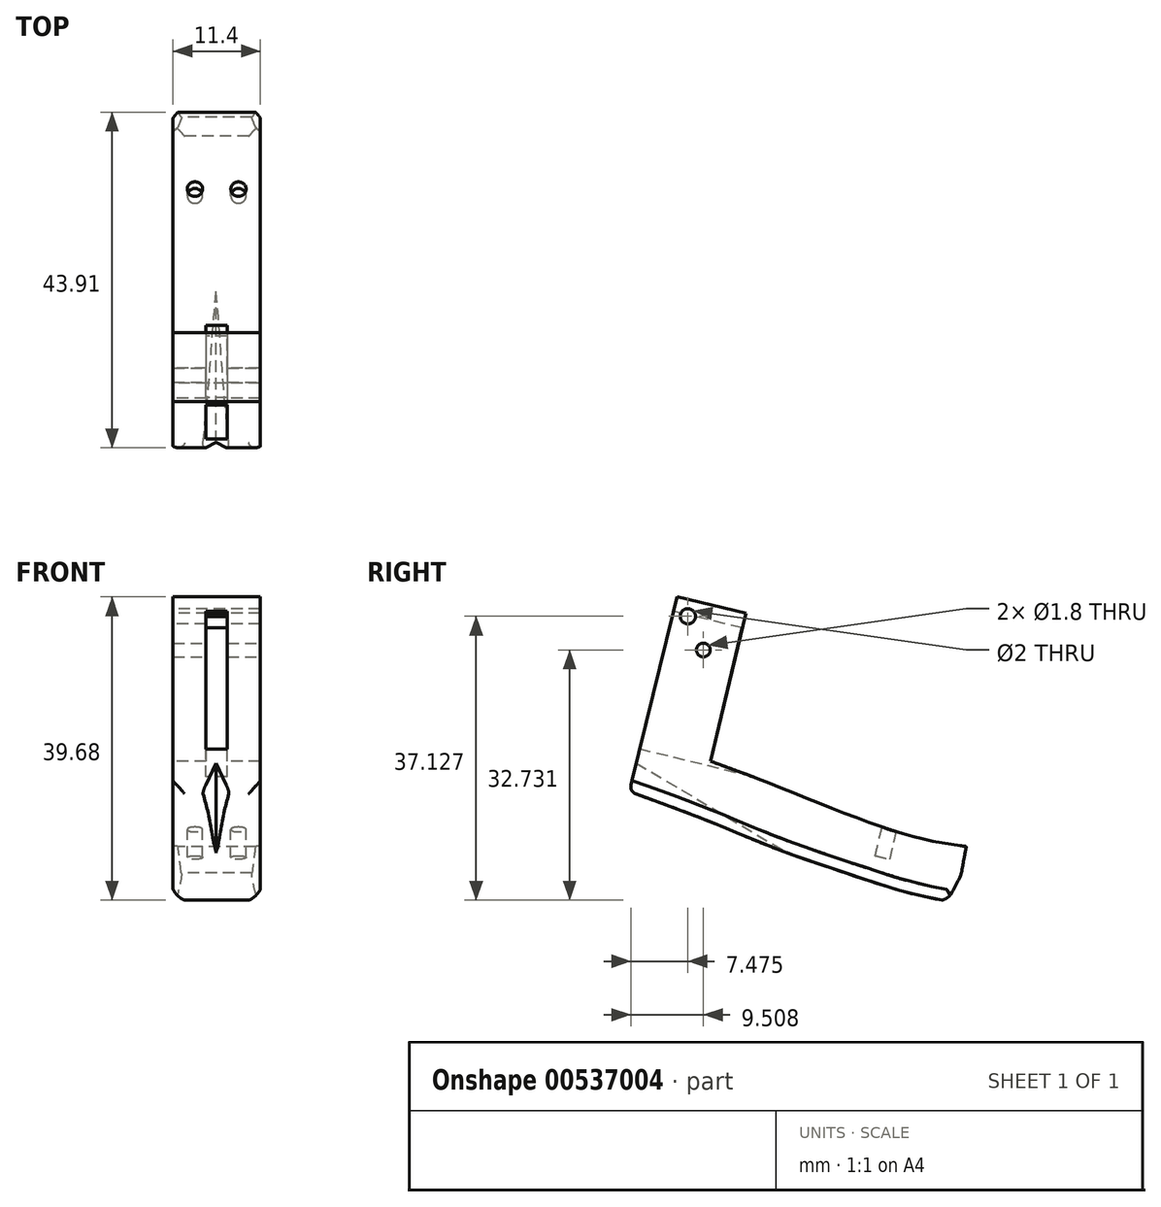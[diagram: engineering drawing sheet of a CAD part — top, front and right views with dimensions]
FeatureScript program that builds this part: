
annotation { "Feature Type Name" : "Feature", "Feature Type Description" : "" }
export const myFeature = defineFeature(function(context is Context, id is Id, definition is map)
    precondition{}
    {
        {
            var Q0;
            Q0=qCreatedBy(makeId("Right.planeOp"),FACE);
            var sketch = newSketch(context, id + "F0", { "sketchPlane" : qUnion([Q0])});
            skLineSegment(sketch, "E0", {"start": v(-10.85, 13.5) * mm, "end": v(-16.58, -9.88) * mm});
            skFitSpline(sketch, "E1", {"points": [v(-16.58, -9.88) * mm, v(-6.61, -13.58) * mm, v(1.68, -16.97) * mm, v(9.59, -19.8) * mm, v(17.55, -22.42) * mm, v(21.87, -23.55) * mm, v(25.94, -24.39) * mm, v(26.4, -22.95) * mm], "startDerivative": vector(48.23, -17.13) * mm, "endDerivative": vector(19.33, 61.07) * mm});
            skLineSegment(sketch, "E2", {"start": v(26.4, -22.95) * mm, "end": v(27.51, -17.06) * mm});
            skFitSpline(sketch, "E3", {"points": [v(27.51, -17.06) * mm, v(20.88, -15.85) * mm, v(10.39, -12.23) * mm, v(-1.4, -7.57) * mm, v(-7.52, -5.36) * mm], "startDerivative": vector(-29.36, 4.09) * mm, "endDerivative": vector(-26.42, 9.18) * mm});
            skLineSegment(sketch, "E4", {"start": v(-10.85, 13.5) * mm, "end": v(-10.35, 15.6) * mm});
            skLineSegment(sketch, "E5", {"start": v(-10.35, 15.6) * mm, "end": v(-1.34, 13.45) * mm});
            skLineSegment(sketch, "E6", {"start": v(-1.34, 13.45) * mm, "end": v(-5.97, -5.9) * mm});
            skCircle(sketch, "E7", {"center": v(-8.93, 13.06) * mm, "radius": 1 * mm});
            skSolve(sketch);
        }
        {
            var Q0;
            Q0=makeQuery(id+"F0.imprint","IMPRINT",FACE,{"disambiguationData":[TD([[makeQuery(id+"F0.imprint","IMPRINT",EDGE,{"derivedFrom":sQuery(id+"F0.wireOp",EDGE,"E0")}),1.0]])]});
            extrude(context, id + "F1", {"entities" : qUnion([Q0]), "depth" : 11.4 * mm, "offsetDistance" : 25 * mm});
        }
        {
            var Q0;
            Q0=makeQuery(id+"F1.opExtrude","SWEPT_FACE",FACE,{"disambiguationData":[OSD([sQuery(id+"F0.wireOp",EDGE,"E0"),sQuery(id+"F0.wireOp",EDGE,"E4")])]});
            var sketch = newSketch(context, id + "F2", { "sketchPlane" : qUnion([Q0])});
            skLineSegment(sketch, "E8", {"start": v(5.7, 10.77) * mm, "end": v(7.1, 10.77) * mm});
            skLineSegment(sketch, "E9", {"start": v(7.1, 10.77) * mm, "end": v(7.1, -7.82) * mm});
            skLineSegment(sketch, "E10", {"start": v(7.1, -7.82) * mm, "end": v(4.3, -7.82) * mm});
            skLineSegment(sketch, "E11", {"start": v(4.3, -7.82) * mm, "end": v(4.3, 10.77) * mm});
            skLineSegment(sketch, "E12", {"start": v(4.3, 10.77) * mm, "end": v(5.7, 10.77) * mm});
            skLineSegment(sketch, "E13", {"start": v(4.3, -5.3) * mm, "end": v(0, -5.3) * mm});
            skSolve(sketch);
        }
        {
            var Q0;
            Q0=makeQuery(id+"F2.imprint","IMPRINT",FACE,{"disambiguationData":[TD([[makeQuery(id+"F2.imprint","IMPRINT",EDGE,{"derivedFrom":sQuery(id+"F2.wireOp",EDGE,"E8")}),-1.0]])]});
            var Q1;
            {var subQ4=sQuery(id+"F2.wireOp",EDGE,"E10");Q1=makeQuery(id+"F2.imprint","IMPRINT",FACE,{"disambiguationData":[TD([[makeQuery(id+"F2.imprint","IMPRINT",EDGE,{"derivedFrom":subQ4}),-1.0]])]});}
            extrude(context, id + "F3", {"entities" : qUnion([Q0, Q1]), "operationType" : NewBodyOperationType.REMOVE, "oppositeDirection" : true, "depth" : 25 * mm, "offsetDistance" : 25 * mm});
        }
        {
            var Q0;
            Q0=makeQuery(id+"F3.boolean.opBoolean","COPY",FACE,{"derivedFrom":makeQuery(id+"F3.opExtrude","SWEPT_FACE",FACE,{"disambiguationData":[OSD([sQuery(id+"F2.wireOp",EDGE,"E11")])]})});
            var sketch = newSketch(context, id + "F4", { "sketchPlane" : qUnion([Q0])});
            skLineSegment(sketch, "E14", {"start": v(-10.8, 13.74) * mm, "end": v(-5.94, 12.55) * mm});
            skLineSegment(sketch, "E15", {"start": v(-5.94, 12.55) * mm, "end": v(-6.9, 8.66) * mm});
            skCircle(sketch, "E16", {"center": v(-6.9, 8.66) * mm, "radius": 0.9 * mm});
            skSolve(sketch);
        }
        {
            var Q0;
            Q0 = qSketchRegion(id + "F4", true);
            extrude(context, id + "F5", {"entities" : qUnion([Q0]), "operationType" : NewBodyOperationType.REMOVE, "endBound" : BoundingType.SYMMETRIC, "oppositeDirection" : true, "depth" : 25 * mm, "offsetDistance" : 25 * mm});
        }
        {
            var Q0;
            Q0=makeQuery(id+"F1.opExtrude","CAP_EDGE",EDGE,{"disambiguationData":[OSD([sQuery(id+"F0.wireOp",EDGE,"E1")])],"isStart":false});
            var Q1;
            Q1=makeQuery(id+"F1.opExtrude","CAP_EDGE",EDGE,{"disambiguationData":[OSD([sQuery(id+"F0.wireOp",EDGE,"E1")])],"isStart":true});
            fillet(context, id + "F6", {"entities" : qUnion([Q0, Q1]), "radius" : 1.5 * mm, "tangentPropagation" : true, "rho" : .1, "crossSection" : FilletCrossSection.CONIC, "allowEdgeOverflow" : false});
        }
        {
            var Q0;
            Q0=makeQuery(id+"F1.opExtrude","SWEPT_EDGE",EDGE,{"disambiguationData":[OSD([sQuery(id+"F0.wireOp",EDGE,"E0"),sQuery(id+"F0.wireOp",EDGE,"E1")])]});
            fillet(context, id + "F7", {"entities" : qUnion([Q0]), "radius" : 1 * mm, "allowEdgeOverflow" : false});
        }
        {
            var Q0;
            Q0=makeQuery(id+"F1.opExtrude","SWEPT_FACE",FACE,{"disambiguationData":[OSD([sQuery(id+"F0.wireOp",EDGE,"E5")])]});
            var sketch = newSketch(context, id + "F8", { "sketchPlane" : qUnion([Q0])});
            skLineSegment(sketch, "E17", {"start": v(5.7, -4.44) * mm, "end": v(5.7, 20.4) * mm});
            skCircle(sketch, "E18", {"center": v(2.85, 20.4) * mm, "radius": 1 * mm});
            skCircle(sketch, "E19", {"center": v(8.55, 20.4) * mm, "radius": 1 * mm});
            skSolve(sketch);
        }
        {
            var Q0;
            Q0 = qSketchRegion(id + "F8", true);
            extrude(context, id + "F9", {"entities" : qUnion([Q0]), "operationType" : NewBodyOperationType.REMOVE, "oppositeDirection" : true, "depth" : 26.9 * mm, "offsetDistance" : 25 * mm});
        }
        {
            var Q0;
            Q0=makeQuery(id+"F1.opExtrude","CAP_FACE",FACE,{"disambiguationData":[OSD([sQuery(id+"F0.wireOp",EDGE,"E0"),sQuery(id+"F0.wireOp",EDGE,"E1"),sQuery(id+"F0.wireOp",EDGE,"E2"),sQuery(id+"F0.wireOp",EDGE,"E3"),sQuery(id+"F0.wireOp",EDGE,"E4"),sQuery(id+"F0.wireOp",EDGE,"E5"),sQuery(id+"F0.wireOp",EDGE,"E6"),sQuery(id+"F0.wireOp",EDGE,"E7")])],"isStart":false});
            var sketch = newSketch(context, id + "F10", { "sketchPlane" : qUnion([Q0])});
            skLineSegment(sketch, "E20", {"start": v(-14.98, -6.24) * mm, "end": v(-8.61, 4.47) * mm});
            skSolve(sketch);
        }
        {
            var Q0;
            Q0=qCreatedBy(makeId("Top.planeOp"),FACE);
            var Q1;
            Q1=sQuery(id+"F10.wireOp",EDGE,"E20");
            cPlane(context, id + "F11", {"entities" : qUnion([Q0, Q1]), "cplaneType" : CPlaneType.LINE_ANGLE, "offset" : 25 * mm, "angle" : 0 * degree, "width" : 150 * mm, "height" : 150 * mm});
        }
        {
            var Q0;
            Q0=qCreatedBy(id+"F11.planeOp",FACE);
            var sketch = newSketch(context, id + "F12", { "sketchPlane" : qUnion([Q0])});
            skLineSegment(sketch, "E21", {"start": v(-5.63, -13.29) * mm, "end": v(-0.99, -22.83) * mm});
            skLineSegment(sketch, "E22", {"start": v(-0.99, -22.83) * mm, "end": v(-11.37, -22.83) * mm});
            skLineSegment(sketch, "E23", {"start": v(-5.63, -13.29) * mm, "end": v(-10.13, -22.83) * mm});
            skSolve(sketch);
        }
        {
            var Q0;
            Q0 = qSketchRegion(id + "F12", true);
            extrude(context, id + "F13", {"entities" : qUnion([Q0]), "operationType" : NewBodyOperationType.REMOVE, "endBound" : BoundingType.SYMMETRIC, "oppositeDirection" : true, "depth" : 149.4 * mm, "offsetDistance" : 25 * mm});
        }
        {
            var Q0;
            Q0=makeQuery(id+"F1.opExtrude","CAP_FACE",FACE,{"disambiguationData":[OSD([sQuery(id+"F0.wireOp",EDGE,"E0"),sQuery(id+"F0.wireOp",EDGE,"E1"),sQuery(id+"F0.wireOp",EDGE,"E2"),sQuery(id+"F0.wireOp",EDGE,"E3"),sQuery(id+"F0.wireOp",EDGE,"E4"),sQuery(id+"F0.wireOp",EDGE,"E5"),sQuery(id+"F0.wireOp",EDGE,"E6"),sQuery(id+"F0.wireOp",EDGE,"E7")])],"isStart":true});
            var sketch = newSketch(context, id + "F14", { "sketchPlane" : qUnion([Q0])});
            skFitSpline(sketch, "E24", {"points": [v(-26.87, -20.46) * mm, v(-25.97, -22.42) * mm, v(-25.08, -23.72) * mm, v(-22.73, -24.43) * mm, v(-19.82, -24.7) * mm], "startDerivative": vector(2.78, -11.09) * mm, "endDerivative": vector(12.87, 0.42) * mm});
            skLineSegment(sketch, "E25", {"start": v(-19.82, -24.7) * mm, "end": v(-19.82, -28.26) * mm});
            skLineSegment(sketch, "E26", {"start": v(-19.82, -28.26) * mm, "end": v(-27.6, -28.26) * mm});
            skLineSegment(sketch, "E27", {"start": v(-27.6, -28.26) * mm, "end": v(-29.13, -20.41) * mm});
            skLineSegment(sketch, "E28", {"start": v(-29.13, -20.41) * mm, "end": v(-26.87, -20.46) * mm});
            skSolve(sketch);
        }
        {
            var Q0;
            Q0=makeQuery(id+"F14.imprint","IMPRINT",FACE,{"disambiguationData":[TD([[makeQuery(id+"F14.imprint","IMPRINT",EDGE,{"derivedFrom":sQuery(id+"F14.wireOp",EDGE,"E24")}),-1.0]])]});
            extrude(context, id + "F15", {"entities" : qUnion([Q0]), "operationType" : NewBodyOperationType.REMOVE, "oppositeDirection" : true, "depth" : 25 * mm, "offsetDistance" : 25 * mm});
        }
    });
